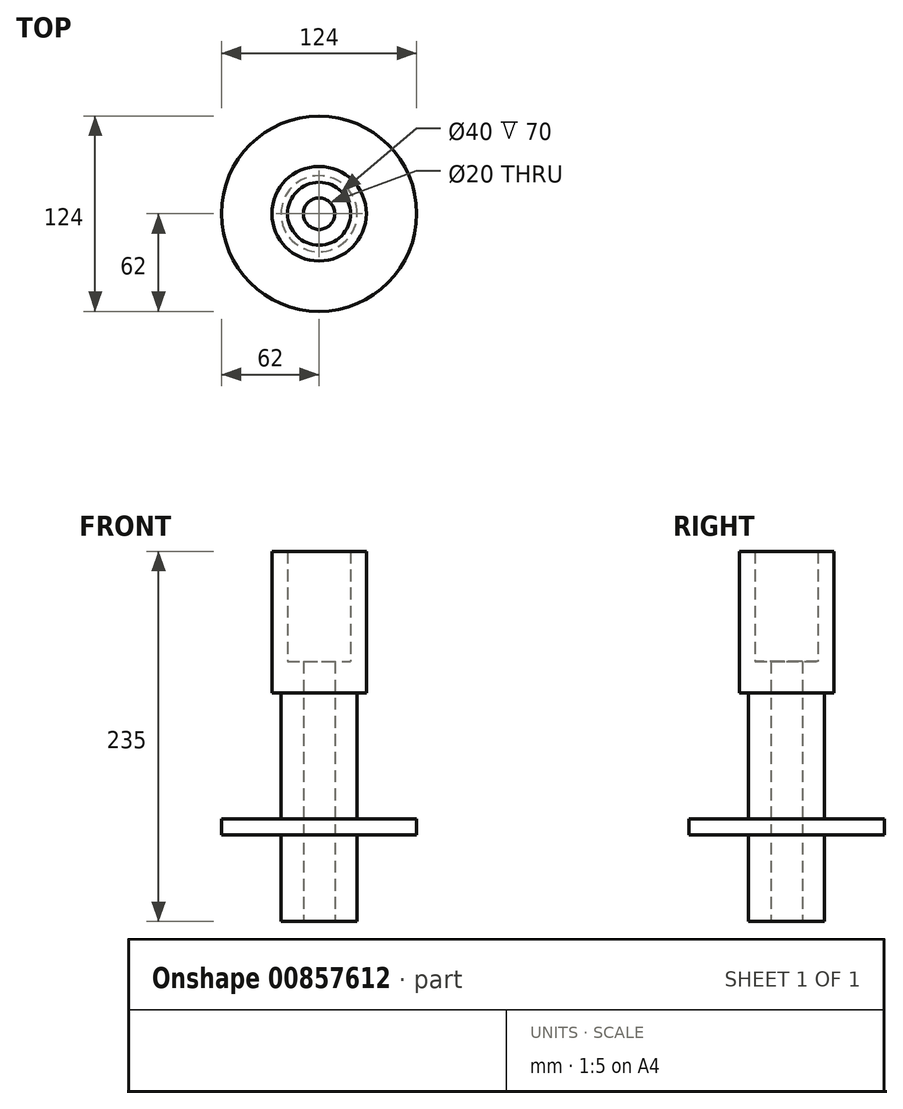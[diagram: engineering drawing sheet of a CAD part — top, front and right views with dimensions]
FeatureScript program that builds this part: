
annotation { "Feature Type Name" : "Feature", "Feature Type Description" : "" }
export const myFeature = defineFeature(function(context is Context, id is Id, definition is map)
    precondition{}
    {
        {
            var Q0;
            Q0=qCreatedBy(makeId("Front.planeOp"),FACE);
            var sketch = newSketch(context, id + "F0", { "sketchPlane" : qUnion([Q0])});
            skLineSegment(sketch, "E0", {"start": v(0, 0) * mm, "end": v(0, 235) * mm, "construction": true});
            skLineSegment(sketch, "E1", {"start": v(10, 0) * mm, "end": v(10, 165) * mm});
            skLineSegment(sketch, "E2", {"start": v(10, 0) * mm, "end": v(24.15, 0) * mm});
            skLineSegment(sketch, "E3", {"start": v(24.15, 0) * mm, "end": v(24.15, 55) * mm});
            skLineSegment(sketch, "E4", {"start": v(24.15, 55) * mm, "end": v(62, 55) * mm});
            skLineSegment(sketch, "E5", {"start": v(62, 55) * mm, "end": v(62, 65) * mm});
            skLineSegment(sketch, "E6", {"start": v(30, 145) * mm, "end": v(30, 235) * mm});
            skLineSegment(sketch, "E7", {"start": v(30, 235) * mm, "end": v(20, 235) * mm});
            skLineSegment(sketch, "E8", {"start": v(20, 235) * mm, "end": v(20, 165) * mm});
            skLineSegment(sketch, "E9", {"start": v(20, 165) * mm, "end": v(10, 165) * mm});
            skLineSegment(sketch, "E10", {"start": v(30, 145) * mm, "end": v(24.15, 145) * mm});
            skLineSegment(sketch, "E11", {"start": v(24.15, 145) * mm, "end": v(24.15, 65) * mm});
            skLineSegment(sketch, "E12", {"start": v(24.15, 65) * mm, "end": v(62, 65) * mm});
            skSolve(sketch);
        }
        {
            var Q0;
            Q0=makeQuery(id+"F0.imprint","IMPRINT",FACE,{"disambiguationData":[TD([[makeQuery(id+"F0.imprint","IMPRINT",EDGE,{"derivedFrom":sQuery(id+"F0.wireOp",EDGE,"E1")}),-1.0]])]});
            var Q1;
            Q1=sQuery(id+"F0.wireOp",EDGE,"E0");
            revolve(context, id + "F1", {"surfaceOperationType" : NewSurfaceOperationType.NEW, "entities" : qUnion([Q0]), "axis" : qUnion([Q1]), "revolveType" : RevolveType.FULL});
        }
    });
